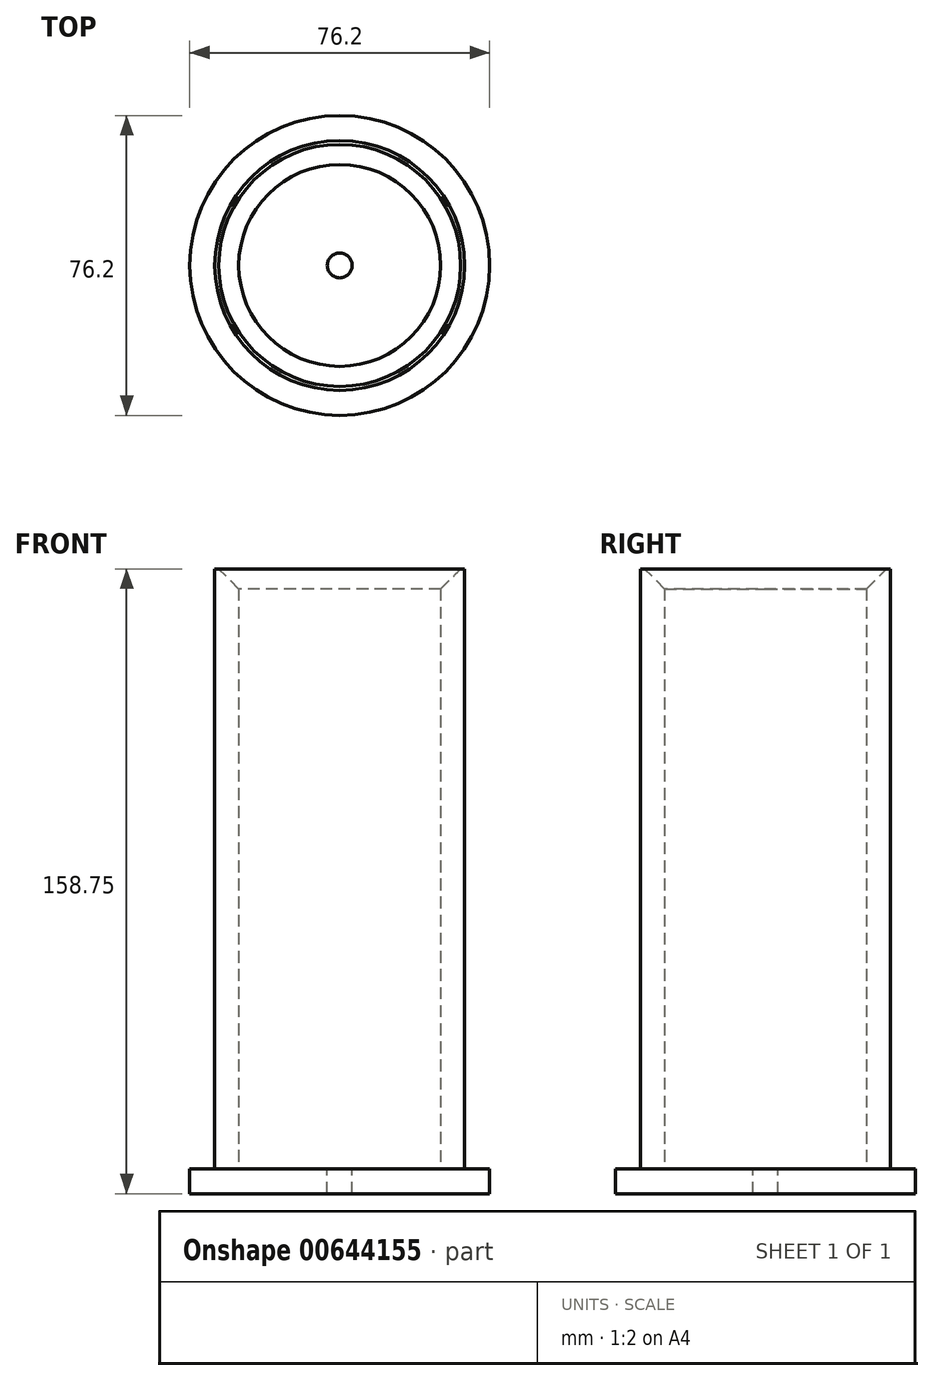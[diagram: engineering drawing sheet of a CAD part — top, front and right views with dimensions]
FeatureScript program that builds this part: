
annotation { "Feature Type Name" : "Feature", "Feature Type Description" : "" }
export const myFeature = defineFeature(function(context is Context, id is Id, definition is map)
    precondition{}
    {
        {
            var Q0;
            Q0=qCreatedBy(makeId("Top.planeOp"),FACE);
            var sketch = newSketch(context, id + "F0", { "sketchPlane" : qUnion([Q0])});
            skCircle(sketch, "E0", {"center": v(0, 0) * mm, "radius": 38.1 * mm});
            skSolve(sketch);
        }
        {
            var Q0;
            Q0=makeQuery(id+"F0.imprint","IMPRINT",FACE,{"disambiguationData":[TD([[makeQuery(id+"F0.imprint","IMPRINT",EDGE,{"derivedFrom":sQuery(id+"F0.wireOp",EDGE,"E0")}),1.0]])]});
            extrude(context, id + "F1", {"entities" : qUnion([Q0]), "depth" : 6.35 * mm, "offsetDistance" : 25.4 * mm});
        }
        {
            var Q0;
            Q0=makeQuery(id+"F1.opExtrude","CAP_FACE",FACE,{"disambiguationData":[OSD([sQuery(id+"F0.wireOp",EDGE,"E0")])],"isStart":false});
            var sketch = newSketch(context, id + "F2", { "sketchPlane" : qUnion([Q0])});
            skCircle(sketch, "E1", {"center": v(0, 0) * mm, "radius": 25.65 * mm});
            skCircle(sketch, "E2", {"center": v(0, 0) * mm, "radius": 31.75 * mm});
            skSolve(sketch);
        }
        {
            var Q0;
            Q0=makeQuery(id+"F2.imprint","IMPRINT",FACE,{"disambiguationData":[TD([[makeQuery(id+"F2.imprint","IMPRINT",EDGE,{"derivedFrom":sQuery(id+"F2.wireOp",EDGE,"E1")}),-1.0]])]});
            extrude(context, id + "F3", {"entities" : qUnion([Q0]), "operationType" : NewBodyOperationType.ADD, "depth" : 152.4 * mm, "offsetDistance" : 25.4 * mm});
        }
        {
            var Q0;
            Q0=makeQuery(id+"F3.boolean.opBoolean","SPLIT",FACE,{"disambiguationData":[TD([makeQuery(id+"F3.opExtrude","SWEPT_FACE",FACE,{"disambiguationData":[OSD([sQuery(id+"F2.wireOp",EDGE,"E1")])]})])],"derivedFrom":makeQuery(id+"F1.opExtrude","CAP_FACE",FACE,{"disambiguationData":[OSD([sQuery(id+"F0.wireOp",EDGE,"E0")])],"isStart":false})});
            var sketch = newSketch(context, id + "F4", { "sketchPlane" : qUnion([Q0])});
            skCircle(sketch, "E3", {"center": v(0, 0) * mm, "radius": 3.18 * mm});
            skSolve(sketch);
        }
        {
            var Q0;
            Q0=makeQuery(id+"F4.imprint","IMPRINT",FACE,{"disambiguationData":[TD([[makeQuery(id+"F4.imprint","IMPRINT",EDGE,{"derivedFrom":sQuery(id+"F4.wireOp",EDGE,"E3")}),1.0]])]});
            extrude(context, id + "F5", {"entities" : qUnion([Q0]), "operationType" : NewBodyOperationType.REMOVE, "oppositeDirection" : true, "depth" : 25.4 * mm, "offsetDistance" : 25.4 * mm});
        }
        {
            var Q0;
            Q0=makeQuery(id+"F3.opExtrude","CAP_EDGE",EDGE,{"disambiguationData":[OSD([sQuery(id+"F2.wireOp",EDGE,"E1")])],"isStart":false});
            chamfer(context, id + "F6", {"entities" : qUnion([Q0]), "width" : 5.08 * mm, "tangentPropagation" : true});
        }
    });
